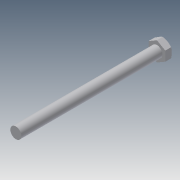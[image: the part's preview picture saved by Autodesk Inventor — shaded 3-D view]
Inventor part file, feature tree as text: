
AUTODESK INVENTOR PART (.ipt)
format: ipt  version: 2014 (Build 180170000, 170)  size: 92,160 bytes
history: native  units: in
note: dims shown in document units (in); Inventor stores cm internally (conversion verified against a paired STEP export)
features: extrude x3, sketch x3
ambient origin geometry x8: Origin, YZ Plane, XZ Plane, XY Plane, X Axis, Y Axis, Z Axis, Center Point
bodies: Solid1 (feature_tree)
feature tree (6):
  extrude  "Extrusion1"  Depth=0.23in TaperAngle=0.0deg
  extrude  "Extrusion2"  Depth=5.0in TaperAngle=0.0deg
  extrude  "Extrusion3"  [1 undecoded]
  sketch  "Sketch1"  dims[d0=0.5625in d1=0.23in d2=0.0in]
  sketch  "Sketch2"  dims[d3=0.375in d4=5.0in d5=0.0in]
  sketch  "Sketch3"  dims[d6=5.0in d7=60.0deg]
note: 1 required parameter value undecoded (feature->parameter linkage not recoverable at this tier; creation-order binding heuristic only, values carry confidence <= 0.55)
